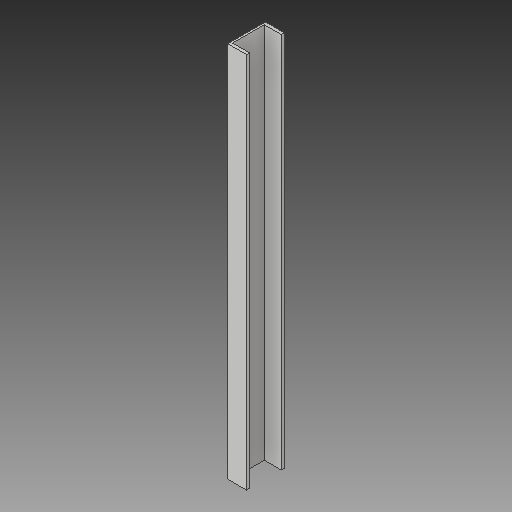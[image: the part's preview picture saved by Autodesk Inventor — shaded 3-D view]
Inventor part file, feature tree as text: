
AUTODESK INVENTOR PART (.ipt)
format: ipt  version: 2019 (Build 230136000, 136)  size: 87,040 bytes
history: native  units: in
note: dims shown in document units (in); Inventor stores cm internally (conversion verified against a paired STEP export)
features: other x3, sketch x1
ambient origin geometry x8: Origin, YZ Plane, XZ Plane, XY Plane, X Axis, Y Axis, Z Axis, Center Point
bodies: Solid1 (feature_tree)
feature tree (4):
  other  "Channel1_MIR1_MIR.ipt"
  other  "Solid1::Channel1_MIR1_MIR.ipt"
  other  "TaggingFeature1"
  sketch  "Sketch1"  dims[d0=0.3937in]
